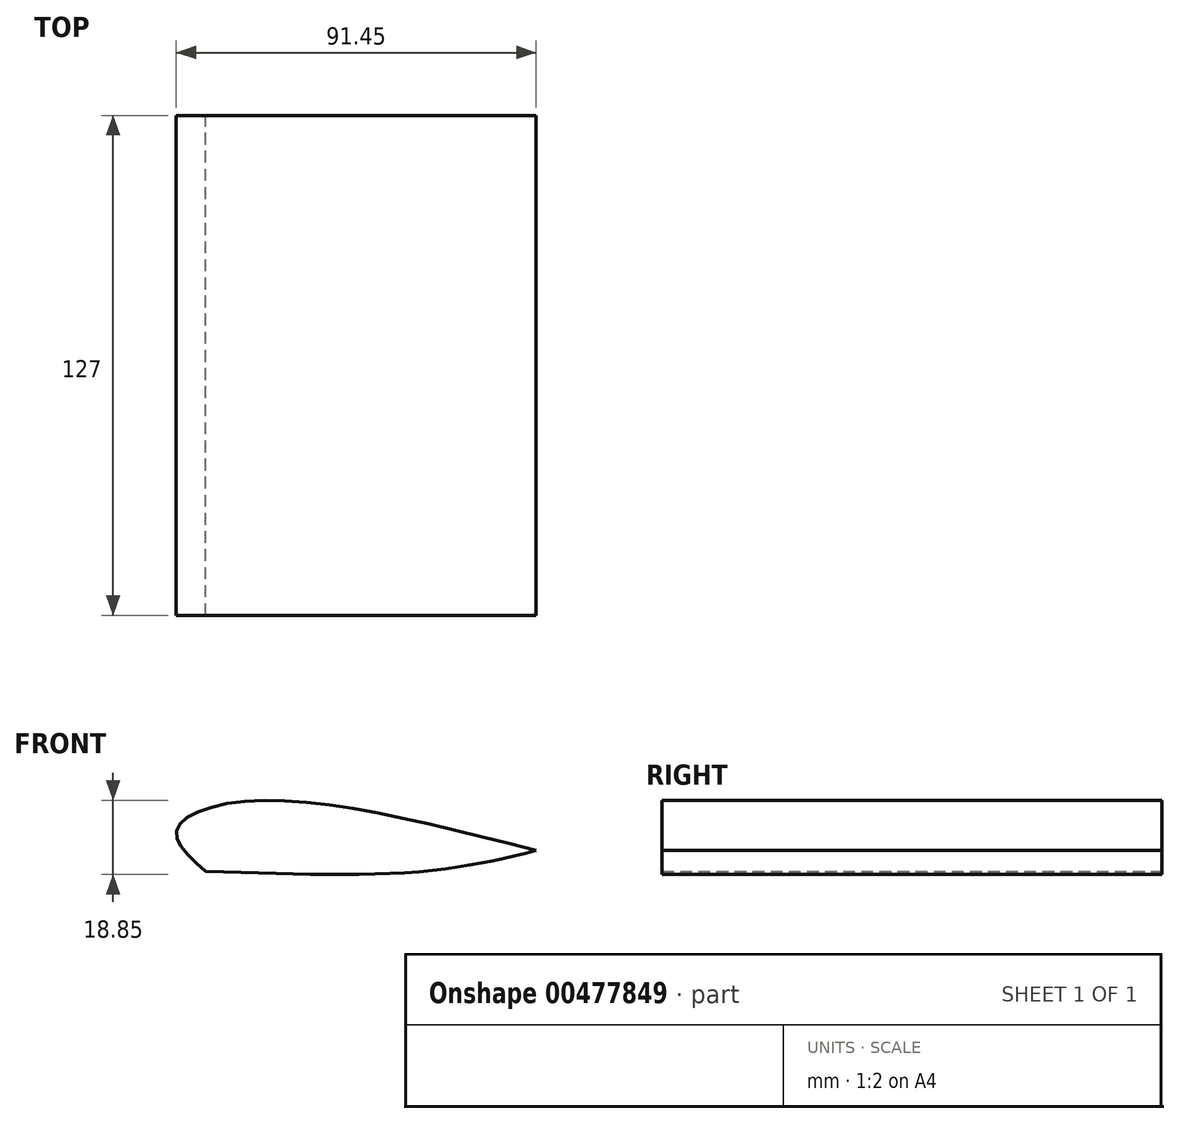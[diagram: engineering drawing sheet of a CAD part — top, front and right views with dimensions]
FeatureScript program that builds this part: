
annotation { "Feature Type Name" : "Feature", "Feature Type Description" : "" }
export const myFeature = defineFeature(function(context is Context, id is Id, definition is map)
    precondition{}
    {
        {
            var Q0;
            Q0=qCreatedBy(makeId("Front.planeOp"),FACE);
            var sketch = newSketch(context, id + "F0", { "sketchPlane" : qUnion([Q0])});
            skFitSpline(sketch, "E0", {"points": [v(-21.37, -5.25) * mm, v(-28.82, 4.78) * mm, v(-11.63, 12.52) * mm, v(62.6, 0) * mm], "startDerivative": vector(-55.53, 48.98) * mm, "endDerivative": vector(158.5, -40.85) * mm});
            skFitSpline(sketch, "E1", {"points": [v(-21.37, -5.25) * mm, v(33.93, -5.25) * mm, v(62.6, 0) * mm], "startDerivative": vector(103.36, -3.62) * mm, "endDerivative": vector(62.4, 15.1) * mm});
            skSolve(sketch);
        }
        {
            var Q0;
            Q0=makeQuery(id+"F0.imprint","IMPRINT",FACE,{"disambiguationData":[TD([[makeQuery(id+"F0.imprint","IMPRINT",EDGE,{"derivedFrom":sQuery(id+"F0.wireOp",EDGE,"E0")}),-1.0]])]});
            extrude(context, id + "F1", {"entities" : qUnion([Q0]), "depth" : 127 * mm});
        }
    });
